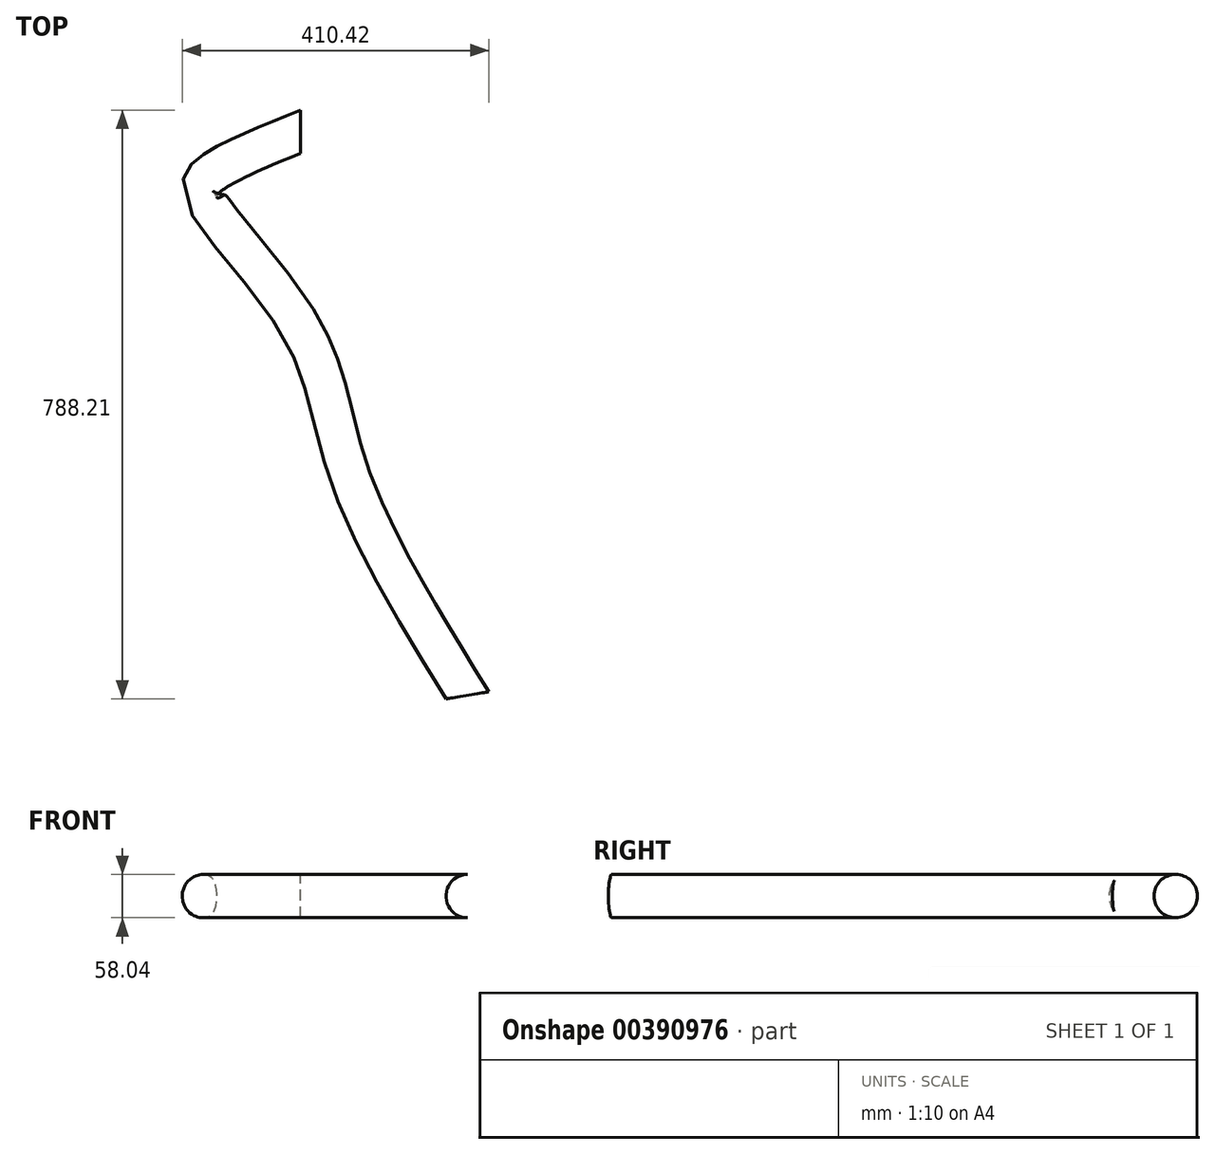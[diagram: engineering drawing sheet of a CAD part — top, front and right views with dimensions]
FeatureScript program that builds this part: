
annotation { "Feature Type Name" : "Feature", "Feature Type Description" : "" }
export const myFeature = defineFeature(function(context is Context, id is Id, definition is map)
    precondition{}
    {
        {
            var Q0;
            Q0=qCreatedBy(makeId("Top.planeOp"),FACE);
            var sketch = newSketch(context, id + "F0", { "sketchPlane" : qUnion([Q0])});
            skFitSpline(sketch, "E0", {"points": [v(0, 0) * mm, v(-115.93, -54.2) * mm, v(-128.74, -82.37) * mm, v(0, -260.83) * mm, v(64.37, -455.35) * mm, v(223.74, -754.48) * mm], "startDerivative": vector(-794.9, -325.12) * mm, "endDerivative": vector(678.56, -1103.46) * mm});
            skSolve(sketch);
        }
        {
            var Q0;
            Q0=qCreatedBy(makeId("Right.planeOp"),FACE);
            var sketch = newSketch(context, id + "F1", { "sketchPlane" : qUnion([Q0])});
            skCircle(sketch, "E1", {"center": v(0, 0) * mm, "radius": 29.02 * mm});
            skSolve(sketch);
        }
        {
            var Q0;
            Q0=makeQuery(id+"F1.imprint","IMPRINT",FACE,{"disambiguationData":[TD([[makeQuery(id+"F1.imprint","IMPRINT",EDGE,{"derivedFrom":sQuery(id+"F1.wireOp",EDGE,"E1")}),1.0]])]});
            var Q1;
            Q1=sQuery(id+"F0.wireOp",EDGE,"E0");
            sweep(context, id + "F2", {"profiles" : qUnion([Q0]), "path" : qUnion([Q1])});
        }
    });
